# Revit family: AF300
name_source: partatom
category: Modelos genéricos
revit_build: Autodesk Revit 2017 (Build: 20181011_1645(x64)
units: mm (PartAtom-declared; Revit-internal decimal feet)

## family parameters
Compartido = No
Corte con vacíos al cargar = No
Cota de conector redondo = Diámetro de uso
Puede alojar armadura = No
Punto de cálculo de habitación = No
Se basa en plano de trabajo = No
Siempre vertical = Sí
Tipo de pieza = Normal

## types (2) — shared parameters
Altura = 730 mm  [stored 2.39501 ft]
Anchura exterior = 362 mm  [stored 1.18766 ft]
Anchura interior = 300 mm  [stored 0.984252 ft]
Clase de carga = F-900 Norma EN-1433
Descripción = Arqueta de Hormigón Polímero tipo ULMA para recogida de aguas pluviales.
Diseño = 2 cuerpos
Fabricante = ULMA Architectural
Ficha técnica = http://www.ulmaarchitectural.com
Longitud = 500 mm  [stored 1.64042 ft]
Peso = 0.00 kg
URL = http://www.ulmaarchitectural.com
Ø salida frontal = 200 mm
Ø salida lateral = 0 mm

## per-type parameters (varying)
| type | Costo | Serie canales |
| AF300S + A300B | 199.46 $ | F300K + SM350F |
| AMF300S + A300B | 227.77 $ | F300MF + SM350MF |

note: column(s) folded — value = type name in every type: Modelo

note: [stored X ft] marks values corroborated as IEEE doubles in the binary element streams (Revit-internal decimal feet)
